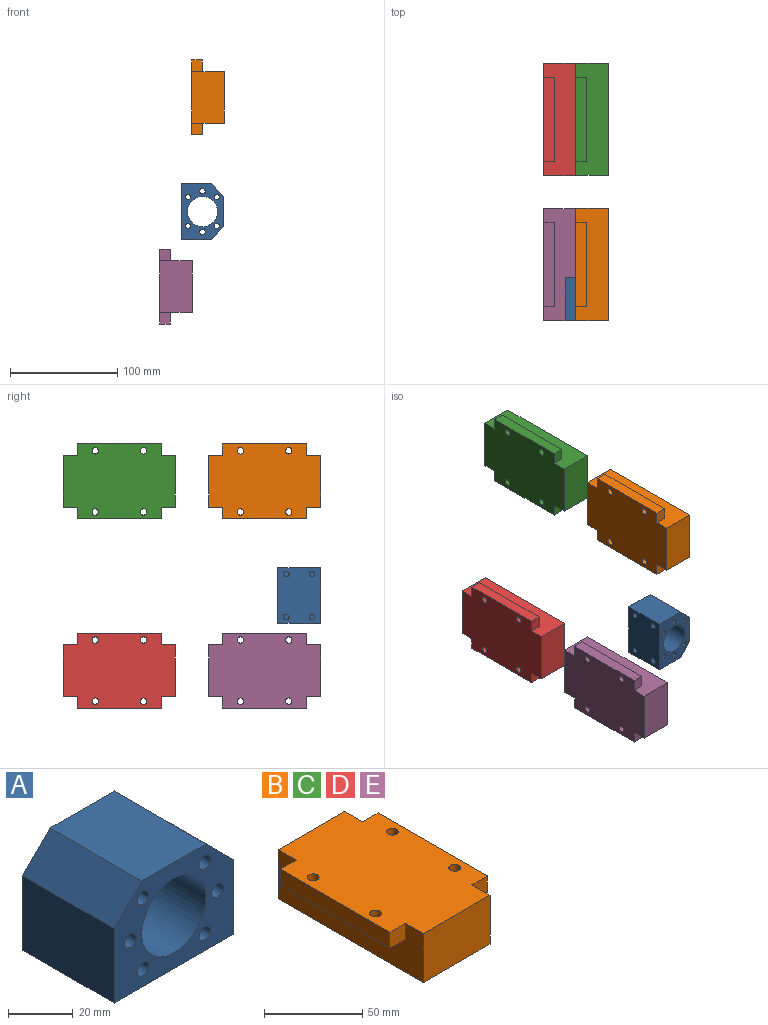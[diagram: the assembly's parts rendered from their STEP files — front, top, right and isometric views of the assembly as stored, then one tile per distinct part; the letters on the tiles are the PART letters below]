
ASSEMBLY  parts=5 mates=3
PART A: 23 faces, bbox 52x40x40 mm
  f0: plane 40x12mm, normal (-0.71,0,0.71), area 678.8mm2, adj f1,f12,f13,f14
  f1: plane 40x28mm, normal (-1,0,0), area 1120mm2, adj f0,f2,f13,f14
  f2: plane 52x40mm, normal (0,0,-1), area 2001.5mm2, adj f1,f3,f13,f14,f15,f17,f19,f21
  f3: plane 40x28mm, normal (1,0,0), area 1120mm2, adj f2,f4,f13,f14
  f4: plane 40x12mm, normal (0.71,0,0.71), area 678.8mm2, adj f3,f12,f13,f14
  f5: cylinder r=14mm len=40mm, axis (0,-1,0), area 3518.6mm2, adj f13,f14
  f6: cylinder r=2.5mm len=40mm, axis (0,-1,0), area 628.3mm2, adj f13,f14
  f7: cylinder r=2.5mm len=40mm, axis (0,-1,0), area 628.3mm2, adj f13,f14
  f8: cylinder r=2.5mm len=40mm, axis (0,-1,0), area 628.3mm2, adj f13,f14
  f9: cylinder r=2.5mm len=40mm, axis (0,-1,0), area 628.3mm2, adj f13,f14
  f10: cylinder r=2.5mm len=40mm, axis (0,-1,0), area 628.3mm2, adj f13,f14
  f11: cylinder r=2.5mm len=40mm, axis (0,-1,0), area 628.3mm2, adj f13,f14
  f12: plane 40x28mm, normal (0,0,1), area 1120mm2, adj f0,f4,f13,f14
  f13: plane 52x40mm, normal (0,1,0), area 1202.4mm2, adj f0,f1,f2,f3,f4,f5,f6,f7
  f14: plane 52x40mm, normal (0,-1,0), area 1202.4mm2, adj f0,f1,f2,f3,f4,f5,f6,f7
  f15: cylinder r=2.5mm len=12mm, axis (0,0,-1), area 188.5mm2, adj f2,f16
  f16: plane 5x5mm, normal (0,0,-1), area 19.6mm2, adj f15
  f17: cylinder r=2.5mm len=12mm, axis (0,0,-1), area 188.5mm2, adj f2,f18
  f18: plane 5x5mm, normal (0,0,-1), area 19.6mm2, adj f17
  f19: cylinder r=2.5mm len=12mm, axis (0,0,-1), area 188.5mm2, adj f2,f20
  f20: plane 5x5mm, normal (0,0,-1), area 19.6mm2, adj f19
  f21: cylinder r=2.5mm len=12mm, axis (0,0,-1), area 188.5mm2, adj f2,f22
  f22: plane 5x5mm, normal (0,0,-1), area 19.6mm2, adj f21
PART B: 18 faces, bbox 70x104.6x30.5 mm
  f0: plane 104.6x70mm, normal (0,0,1), area 6636.9mm2, adj f1,f3,f4,f5,f6,f7,f8,f10
  f1: plane 104.6x30.5mm, normal (-1,0,0), area 2404.3mm2, adj f0,f2,f4,f5,f12,f13,f14
  f2: plane 104.6x48mm, normal (0,0,-1), area 5020.8mm2, adj f1,f3,f4,f5
  f3: plane 104.6x30.5mm, normal (1,0,0), area 2404.3mm2, adj f0,f2,f4,f5,f9,f10,f11
  f4: plane 48x30.5mm, normal (0,1,0), area 1464mm2, adj f0,f1,f2,f3
  f5: plane 48x30.5mm, normal (0,-1,0), area 1464mm2, adj f0,f1,f2,f3
  f6: plane 78.6x10mm, normal (1,0,0), area 786mm2, adj f0,f9,f10,f11
  f7: cylinder r=3mm len=10mm, axis (0,0,1), area 188.5mm2, adj f0,f9
  f8: cylinder r=3mm len=10mm, axis (0,0,1), area 188.5mm2, adj f0,f9
  f9: plane 78.6x11mm, normal (0,0,-1), area 808.1mm2, adj f3,f6,f7,f8,f10,f11
  f10: plane 11x10mm, normal (0,1,0), area 110mm2, adj f0,f3,f6,f9
  f11: plane 11x10mm, normal (0,-1,0), area 110mm2, adj f0,f3,f6,f9
  f12: plane 78.6x11mm, normal (0,0,-1), area 808.1mm2, adj f1,f13,f14,f15,f16,f17
  f13: plane 11x10mm, normal (0,-1,0), area 110mm2, adj f0,f1,f12,f16
  f14: plane 11x10mm, normal (0,1,0), area 110mm2, adj f0,f1,f12,f16
  f15: cylinder r=3mm len=10mm, axis (0,0,1), area 188.5mm2, adj f0,f12
  f16: plane 78.6x10mm, normal (-1,0,0), area 786mm2, adj f0,f12,f13,f14
  f17: cylinder r=3mm len=10mm, axis (0,0,1), area 188.5mm2, adj f0,f12
PART C: same geometry as B
PART D: same geometry as B
PART E: same geometry as B
PLACE A rot(axis=(0.71,0,0.71),180deg) t=(-157.46,-44.93,58.24)mm
PLACE B rot(axis=(0,-1,0),90deg) t=(-152.21,-84.93,164.74)mm
PLACE C rot(axis=(0,-1,0),90deg) t=(-152.21,50.47,164.74)mm
PLACE D rot(axis=(0,-1,0),90deg) t=(-182.21,50.47,-11.76)mm
PLACE E rot(axis=(0,-1,0),90deg) t=(-182.21,-84.93,-11.76)mm
MATE planar D.f4 <-> C.f4  axis (0,1,0) through (-182.21,155.07,-11.76)mm
MATE planar D.f3 <-> E.f3  axis (0,0,1) through (-178.86,102.77,12.24)mm
MATE planar C.f3 <-> B.f3  axis (0,0,1) through (-148.86,102.77,188.74)mm
